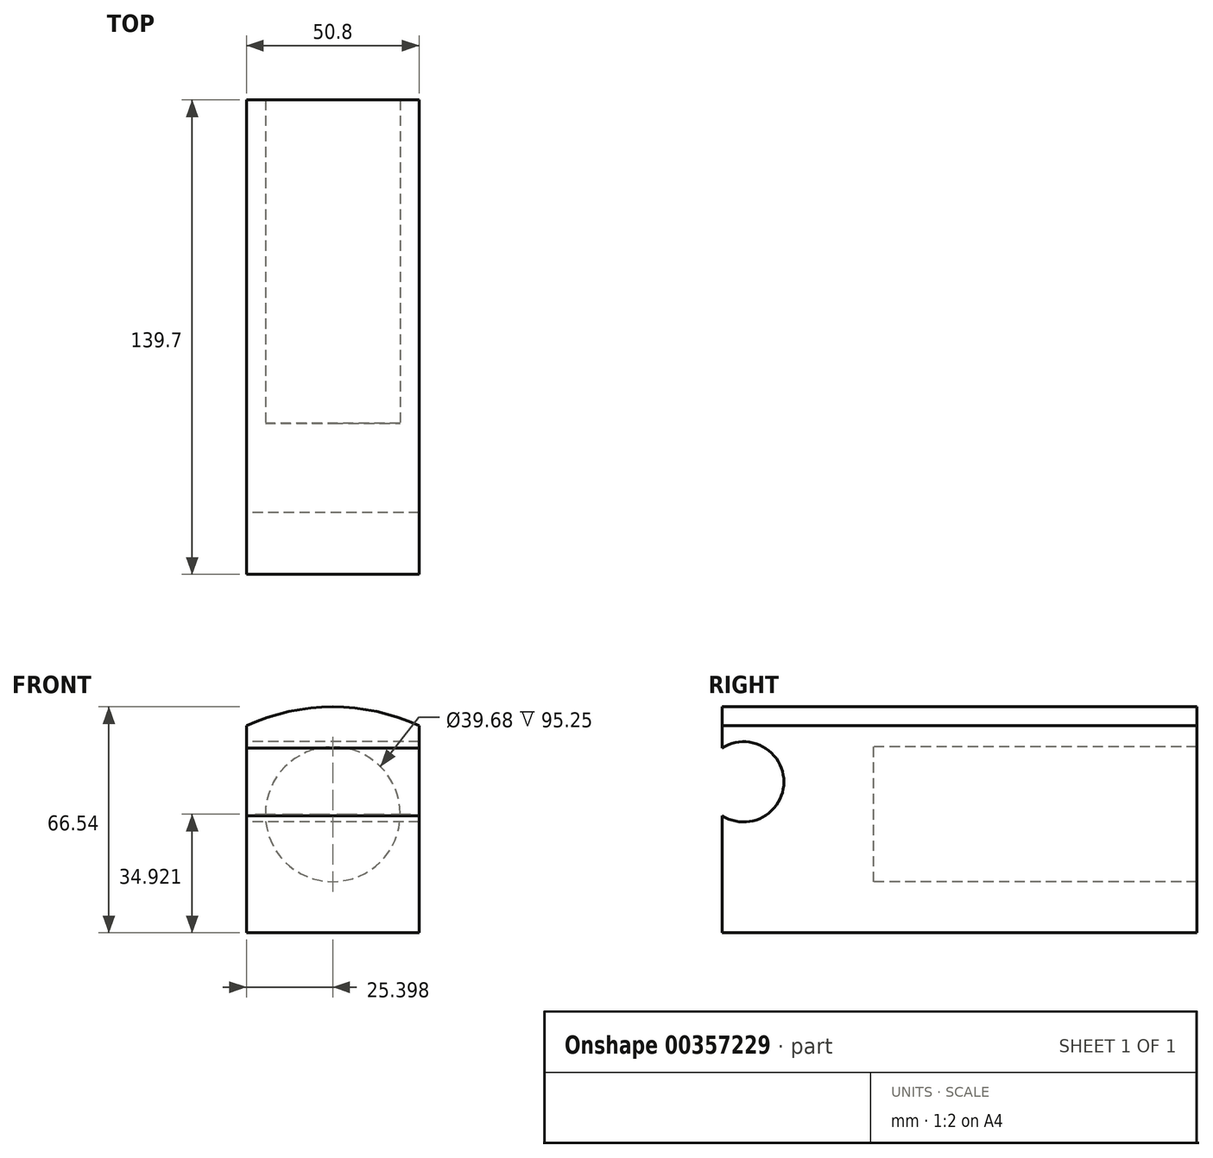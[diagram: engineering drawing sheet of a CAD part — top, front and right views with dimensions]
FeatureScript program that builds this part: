
annotation { "Feature Type Name" : "Feature", "Feature Type Description" : "" }
export const myFeature = defineFeature(function(context is Context, id is Id, definition is map)
    precondition{}
    {
        {
            var Q0;
            Q0=qCreatedBy(makeId("Front.planeOp"),FACE);
            var sketch = newSketch(context, id + "F0", { "sketchPlane" : qUnion([Q0])});
            skLineSegment(sketch, "E0", {"start": v(18.73, -23.5) * mm, "end": v(-32.07, -23.5) * mm});
            skLineSegment(sketch, "E1", {"start": v(18.73, -23.5) * mm, "end": v(18.73, 37.47) * mm});
            skLineSegment(sketch, "E2", {"start": v(-32.07, -23.5) * mm, "end": v(-32.07, 37.47) * mm});
            skArc(sketch, "E3", {"start": v(18.73, 37.47) * mm, "mid": v(-6.67, 43.05) * mm, "end": v(-32.07, 37.47) * mm});
            skSolve(sketch);
        }
        {
            var Q0;
            Q0=makeQuery(id+"F0.imprint","IMPRINT",FACE,{"disambiguationData":[TD([[makeQuery(id+"F0.imprint","IMPRINT",EDGE,{"derivedFrom":sQuery(id+"F0.wireOp",EDGE,"E0")}),-1.0]])]});
            extrude(context, id + "F1", {"entities" : qUnion([Q0]), "depth" : 44.45 * mm});
        }
        {
            var Q0;
            Q0=makeQuery(id+"F1.opExtrude","SWEPT_FACE",FACE,{"disambiguationData":[OSD([sQuery(id+"F0.wireOp",EDGE,"E2")])]});
            var sketch = newSketch(context, id + "F2", { "sketchPlane" : qUnion([Q0])});
            skCircle(sketch, "E4", {"center": v(38.1, 20.96) * mm, "radius": 11.82 * mm});
            skSolve(sketch);
        }
        {
            var Q0;
            {var subQ0=sQuery(id+"F2.wireOp",EDGE,"E4");var subQ1=makeQuery(id+"F1.opExtrude","CAP_EDGE",EDGE,{"disambiguationData":[OSD([sQuery(id+"F0.wireOp",EDGE,"E2")])],"isStart":false});var subQ2=makeQuery(id+"F2.imprint","INTERSECT",VERTEX,{"disambiguationData":[OD(0.0)],"derivedFrom":[subQ1,subQ0]});Q0=makeQuery(id+"F2.imprint","IMPRINT",FACE,{"disambiguationData":[TD([[makeQuery(id+"F2.imprint","IMPRINT",EDGE,{"disambiguationData":[TD([[subQ2,1.0]])],"derivedFrom":subQ0}),1.0]])]});}
            extrude(context, id + "F3", {"entities" : qUnion([Q0]), "operationType" : NewBodyOperationType.REMOVE, "oppositeDirection" : true, "depth" : 50.8 * mm});
        }
        {
            var Q0;
            Q0=makeQuery(id+"F1.opExtrude","CAP_FACE",FACE,{"disambiguationData":[OSD([sQuery(id+"F0.wireOp",EDGE,"E0"),sQuery(id+"F0.wireOp",EDGE,"E1"),sQuery(id+"F0.wireOp",EDGE,"E2"),sQuery(id+"F0.wireOp",EDGE,"E3")])],"isStart":true});
            var sketch = newSketch(context, id + "F4", { "sketchPlane" : qUnion([Q0])});
            skLineSegment(sketch, "E5.bottom", {"start": v(-18.73, -23.5) * mm, "end": v(32.07, -23.5) * mm});
            skLineSegment(sketch, "E5.top", {"start": v(-18.73, -1.28) * mm, "end": v(32.07, -1.28) * mm});
            skLineSegment(sketch, "E5.left", {"start": v(-18.73, -23.5) * mm, "end": v(-18.73, -1.28) * mm});
            skLineSegment(sketch, "E5.right", {"start": v(32.07, -23.5) * mm, "end": v(32.07, -1.28) * mm});
            skCircle(sketch, "E6", {"center": v(6.67, 11.43) * mm, "radius": 19.84 * mm});
            skSolve(sketch);
        }
        {
            var Q0;
            {var subQ0=sQuery(id+"F4.wireOp",EDGE,"E6");var subQ1=sQuery(id+"F4.wireOp",EDGE,"E5.top");var subQ2=makeQuery(id+"F4.imprint","INTERSECT",VERTEX,{"disambiguationData":[OD(0.0)],"derivedFrom":[subQ1,subQ0]});Q0=makeQuery(id+"F4.imprint","IMPRINT",FACE,{"disambiguationData":[TD([[makeQuery(id+"F4.imprint","IMPRINT",EDGE,{"disambiguationData":[TD([[subQ2,-1.0]])],"derivedFrom":subQ1}),1.0]])]});}
            var Q1;
            Q1=makeQuery(id+"F4.imprint","IMPRINT",FACE,{"disambiguationData":[TD([[makeQuery(id+"F4.imprint","IMPRINT",EDGE,{"derivedFrom":sQuery(id+"F4.wireOp",EDGE,"E5.bottom")}),1.0]])]});
            var Q2;
            {var subQ0=sQuery(id+"F4.wireOp",EDGE,"E6");var subQ1=sQuery(id+"F4.wireOp",EDGE,"E5.top");var subQ2=makeQuery(id+"F4.imprint","INTERSECT",VERTEX,{"disambiguationData":[OD(0.0)],"derivedFrom":[subQ1,subQ0]});Q2=makeQuery(id+"F4.imprint","IMPRINT",FACE,{"disambiguationData":[TD([[makeQuery(id+"F4.imprint","IMPRINT",EDGE,{"disambiguationData":[TD([[subQ2,-1.0]])],"derivedFrom":subQ1}),-1.0]])]});}
            extrude(context, id + "F5", {"entities" : qUnion([Q0, Q1, Q2]), "operationType" : NewBodyOperationType.ADD, "depth" : 95.25 * mm});
        }
    });
